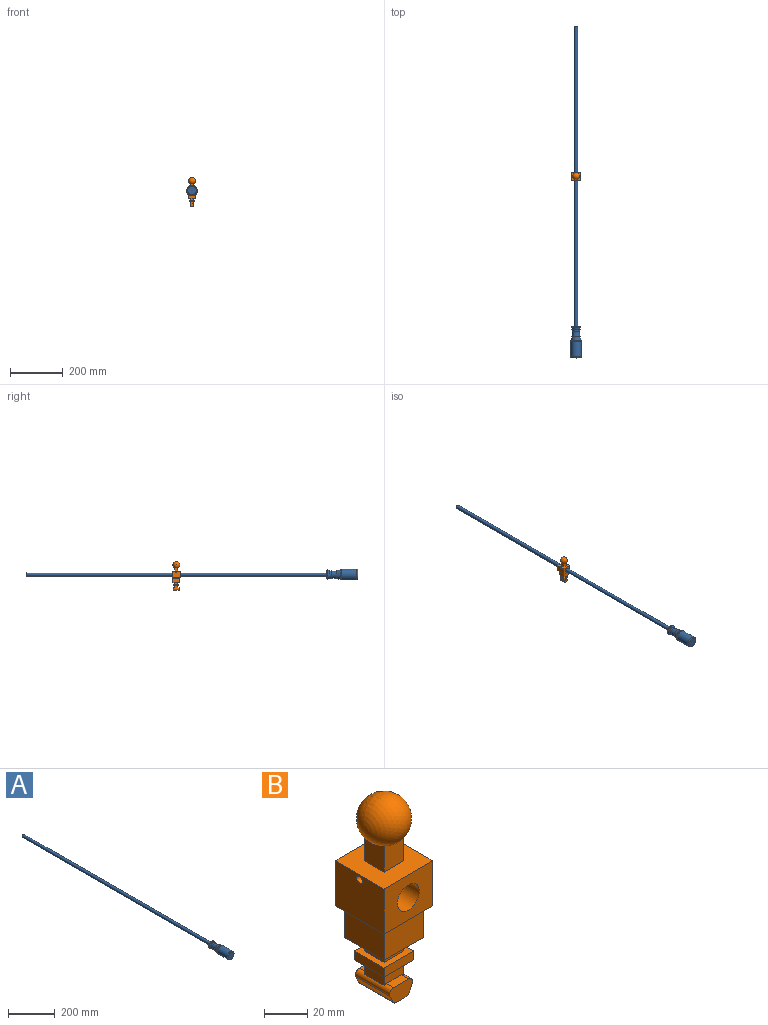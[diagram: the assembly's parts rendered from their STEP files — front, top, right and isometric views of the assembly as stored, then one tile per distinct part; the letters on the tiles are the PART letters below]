
ASSEMBLY  parts=2 mates=1
PART A: 12 faces, bbox 192.8x1262.4x192.8 mm
  f0: cylinder r=6.99mm len=1143mm, axis (0,-1,0), area 50164mm2, adj f1,f11
  f1: plane 13.97x13.97mm, normal (0,1,0), area 153.3mm2, adj f0
  f2: plane 33.02x33.02mm, normal (0,-1,0), area 856.3mm2, adj f3
  f3: torus R=16.51mm, axis (0,-1,0), area 712mm2, adj f2,f4
  f4: cylinder r=20.32mm len=57.12mm, axis (0,-1,0), area 7292.3mm2, adj f3,f5
  f5: revolved ~40.64x40.64mm, area 910.3mm2, adj f4,f6
  f6: torus R=122.92mm, axis (0,-1,0), area 1637.7mm2, adj f5,f7
  f7: torus R=101.43mm, axis (0,-1,0), area 1622.5mm2, adj f6,f8
  f8: torus R=39.47mm, axis (0,-1,0), area 660.1mm2, adj f7,f9
  f9: torus R=305.49mm, axis (0,-1,0), area 719mm2, adj f8,f10
  f10: torus R=13.9mm, axis (0,-1,0), area 754.8mm2, adj f9,f11
  f11: plane 27.8x27.8mm, normal (0,1,0), area 453.7mm2, adj f0,f10
PART B: 48 faces, bbox 31.8x31.8x109.2 mm
  f0: plane 9.93x4.76mm, normal (0,0,1), area 47.3mm2, adj f27,f31,f43,f46
  f1: plane 25.4x25.4mm, normal (0,0,-1), area 483.9mm2, adj f14,f15,f16,f17,f18,f19,f20,f21
  f2: plane 31.75x31.75mm, normal (0,0,-1), area 645.2mm2, adj f4,f6,f7,f8,f9,f10,f11,f12
  f3: plane 31.75x31.75mm, normal (0,0,1), area 846.8mm2, adj f4,f6,f7,f8,f38,f39,f40,f41
  f4: plane 31.75x25.4mm, normal (-1,0,0), area 795mm2, adj f2,f3,f7,f8,f47
  f5: cylinder r=7.14mm len=31.75mm, axis (0,1,0), area 1425.1mm2, adj f7,f8
  f6: plane 31.75x25.4mm, normal (1,0,0), area 795mm2, adj f2,f3,f7,f8,f47
  f7: plane 31.75x25.4mm, normal (0,-1,0), area 646.1mm2, adj f2,f3,f4,f5,f6
  f8: plane 31.75x25.4mm, normal (0,1,0), area 646.1mm2, adj f2,f3,f4,f5,f6
  f9: plane 19.05x2.54mm, normal (1,0,0), area 48.4mm2, adj f2,f11,f12,f13
  f10: plane 19.05x2.54mm, normal (-1,0,0), area 48.4mm2, adj f2,f11,f12,f13
  f11: plane 19.05x2.54mm, normal (0,-1,0), area 48.4mm2, adj f2,f9,f10,f13
  f12: plane 19.05x2.54mm, normal (0,1,0), area 48.4mm2, adj f2,f9,f10,f13
  f13: plane 25.4x25.4mm, normal (0,0,1), area 282.3mm2, adj f9,f10,f11,f12,f14,f15,f16,f17
  f14: plane 25.4x15.24mm, normal (-1,0,0), area 387.1mm2, adj f1,f13,f16,f17
  f15: plane 25.4x15.24mm, normal (1,0,0), area 387.1mm2, adj f1,f13,f16,f17
  f16: plane 25.4x15.24mm, normal (0,-1,0), area 387.1mm2, adj f1,f13,f14,f15
  f17: plane 25.4x15.24mm, normal (0,1,0), area 387.1mm2, adj f1,f13,f14,f15
  f18: plane 12.7x7.62mm, normal (1,0,0), area 96.8mm2, adj f1,f20,f21,f34
  f19: plane 12.7x7.62mm, normal (-1,0,0), area 96.8mm2, adj f1,f20,f21,f34
  f20: plane 12.7x7.62mm, normal (0,-1,0), area 96.8mm2, adj f1,f18,f19,f34
  f21: plane 12.7x7.62mm, normal (0,1,0), area 96.8mm2, adj f1,f18,f19,f34
  f22: plane 9.93x4.76mm, normal (0,0,1), area 47.3mm2, adj f26,f30,f43,f46
  f23: plane 22.23x4.12mm, normal (-0.91,0,-0.41), area 100.4mm2, adj f26,f27,f43,f44
  f24: plane 22.23x6.24mm, normal (0,0,-1), area 138.6mm2, adj f26,f27,f44,f45
  f25: plane 22.23x4.12mm, normal (0.91,0,-0.41), area 100.4mm2, adj f26,f27,f45,f46
  f26: plane 15.01x9.2mm, normal (0,-1,0), area 117.6mm2, adj f22,f23,f24,f25,f43,f44,f45,f46
  f27: plane 15.01x9.2mm, normal (0,1,0), area 117.6mm2, adj f0,f23,f24,f25,f43,f44,f45,f46
  f28: plane 12.7x8.03mm, normal (1,0,0), area 102mm2, adj f30,f31,f32,f46
  f29: plane 12.7x8.03mm, normal (-1,0,0), area 102mm2, adj f30,f31,f32,f43
  f30: plane 12.7x8.03mm, normal (0,-1,0), area 97.1mm2, adj f22,f28,f29,f32,f43,f46
  f31: plane 12.7x8.03mm, normal (0,1,0), area 97.1mm2, adj f0,f28,f29,f32,f43,f46
  f32: plane 19.05x19.05mm, normal (0,0,-1), area 201.6mm2, adj f28,f29,f30,f31,f33,f35,f36,f37
  f33: plane 19.05x5.08mm, normal (1,0,0), area 96.8mm2, adj f32,f34,f36,f37
  f34: plane 19.05x19.05mm, normal (0,0,1), area 201.6mm2, adj f18,f19,f20,f21,f33,f35,f36,f37
  f35: plane 19.05x5.08mm, normal (-1,0,0), area 96.8mm2, adj f32,f34,f36,f37
  f36: plane 19.05x5.08mm, normal (0,-1,0), area 96.8mm2, adj f32,f33,f34,f35
  f37: plane 19.05x5.08mm, normal (0,1,0), area 96.8mm2, adj f32,f33,f34,f35
  f38: plane 14.84x12.7mm, normal (0,1,0), area 171mm2, adj f3,f39,f40,f42
  f39: plane 14.84x12.7mm, normal (-1,0,0), area 171mm2, adj f3,f38,f41,f42
  f40: plane 14.84x12.7mm, normal (1,0,0), area 171mm2, adj f3,f38,f41,f42
  f41: plane 14.84x12.7mm, normal (0,-1,0), area 171mm2, adj f3,f39,f40,f42
  f42: sphere r=12.7mm, area 1849mm2, adj f38,f39,f40,f41
  f43: cylinder r=2.54mm len=22.23mm, axis (0,1,0), area 93.9mm2, adj f0,f22,f23,f26,f27,f29,f30,f31
  f44: cylinder r=2.54mm len=22.23mm, axis (0,-1,0), area 64.9mm2, adj f23,f24,f26,f27
  f45: cylinder r=2.54mm len=22.23mm, axis (0,1,0), area 64.9mm2, adj f24,f25,f26,f27
  f46: cylinder r=2.54mm len=22.23mm, axis (0,-1,0), area 93.9mm2, adj f0,f22,f25,f26,f27,f28,f30,f31
  f47: cylinder r=1.91mm len=31.75mm, axis (1,0,0), area 380mm2, adj f4,f6
PLACE A t=(-630,-517.27,-183.77)mm
PLACE B t=(-630,54.23,-147.25)mm
MATE fastened B.f5 <-> A.f0  axis (0,1,0) through (-630,54.23,-183.77)mm
